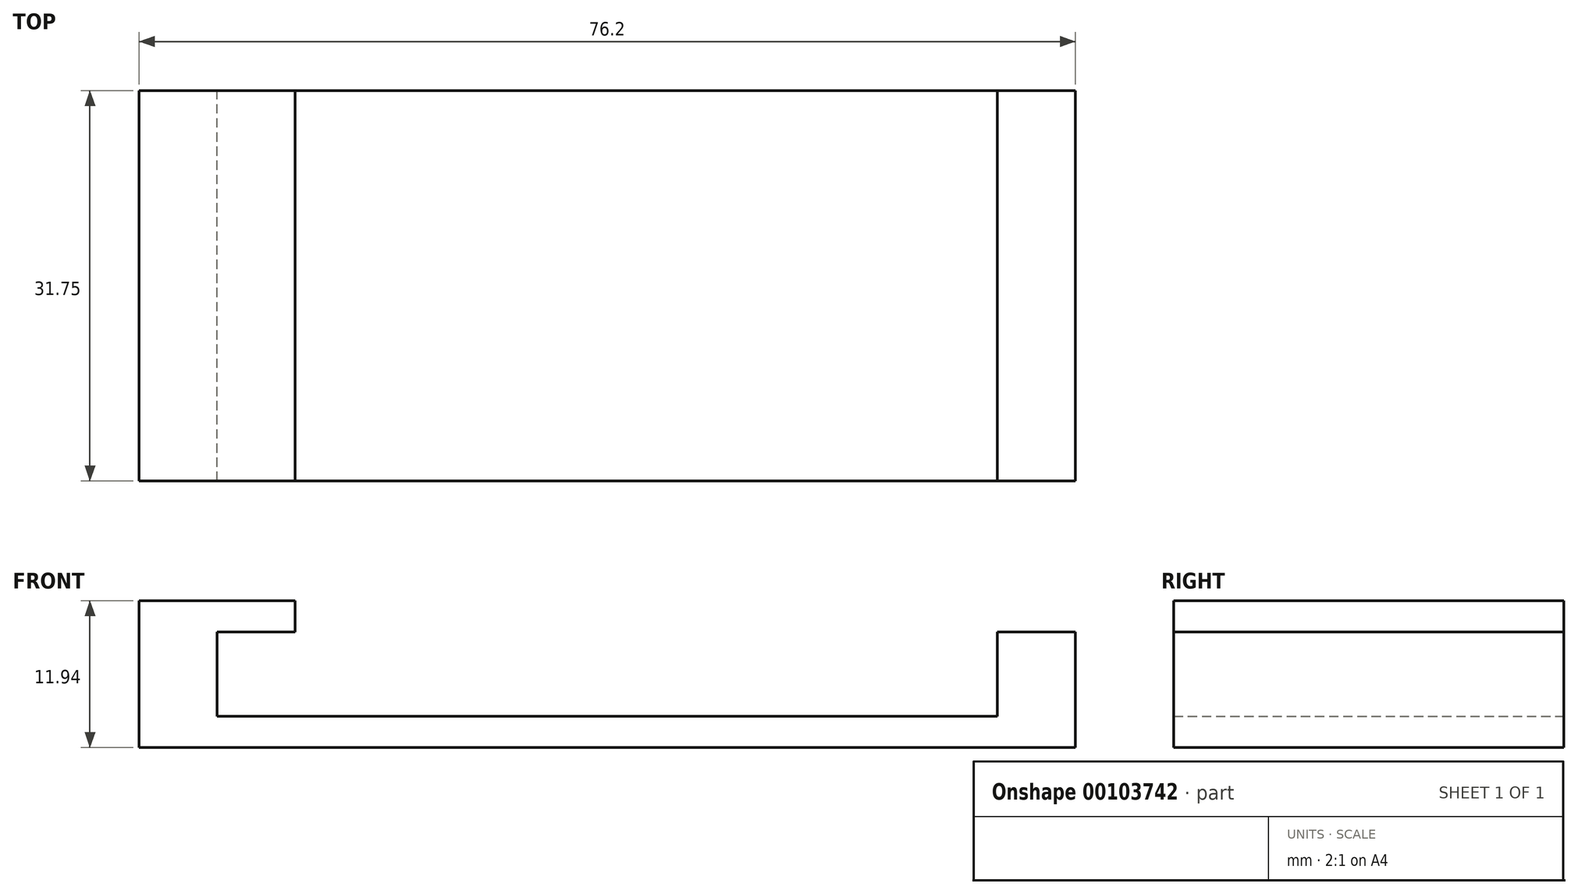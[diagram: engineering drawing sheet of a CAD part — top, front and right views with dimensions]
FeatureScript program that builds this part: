
annotation { "Feature Type Name" : "Feature", "Feature Type Description" : "" }
export const myFeature = defineFeature(function(context is Context, id is Id, definition is map)
    precondition{}
    {
        {
            var Q0;
            Q0=qCreatedBy(makeId("Top.planeOp"),FACE);
            var sketch = newSketch(context, id + "F0", { "sketchPlane" : qUnion([Q0])});
            skLineSegment(sketch, "E0.bottom", {"start": v(-31.75, 31.75) * mm, "end": v(31.75, 31.75) * mm});
            skLineSegment(sketch, "E0.top", {"start": v(-31.75, 0) * mm, "end": v(31.75, 0) * mm});
            skLineSegment(sketch, "E0.left", {"start": v(-31.75, 31.75) * mm, "end": v(-31.75, 0) * mm});
            skLineSegment(sketch, "E0.right", {"start": v(31.75, 31.75) * mm, "end": v(31.75, 0) * mm});
            skLineSegment(sketch, "E1.0", {"start": v(38.1, 31.75) * mm, "end": v(38.1, 0) * mm});
            skLineSegment(sketch, "E2.0", {"start": v(-38.1, 31.75) * mm, "end": v(-38.1, 0) * mm});
            skLineSegment(sketch, "E3", {"start": v(-38.1, 31.75) * mm, "end": v(-31.75, 31.75) * mm});
            skLineSegment(sketch, "E4", {"start": v(-38.1, 0) * mm, "end": v(-31.75, 0) * mm});
            skLineSegment(sketch, "E5", {"start": v(31.75, 0) * mm, "end": v(38.1, 0) * mm});
            skLineSegment(sketch, "E6", {"start": v(31.75, 31.75) * mm, "end": v(38.1, 31.75) * mm});
            skPoint(sketch, "E7", {"position": v(-38.1, 15.87) * mm});
            skPoint(sketch, "E8", {"position": v(-31.75, 15.87) * mm});
            skSolve(sketch);
        }
        {
            var Q0;
            Q0=makeQuery(id+"F0.imprint","IMPRINT",FACE,{"disambiguationData":[TD([[makeQuery(id+"F0.imprint","IMPRINT",EDGE,{"derivedFrom":sQuery(id+"F0.wireOp",EDGE,"E0.left")}),-1.0]])]});
            var Q1;
            Q1=makeQuery(id+"F0.imprint","IMPRINT",FACE,{"disambiguationData":[TD([[makeQuery(id+"F0.imprint","IMPRINT",EDGE,{"derivedFrom":sQuery(id+"F0.wireOp",EDGE,"E0.bottom")}),-1.0]])]});
            var Q2;
            Q2=makeQuery(id+"F0.imprint","IMPRINT",FACE,{"disambiguationData":[TD([[makeQuery(id+"F0.imprint","IMPRINT",EDGE,{"derivedFrom":sQuery(id+"F0.wireOp",EDGE,"E0.right")}),1.0]])]});
            extrude(context, id + "F1", {"entities" : qUnion([Q0, Q1, Q2]), "depth" : 2.54 * mm});
        }
        {
            var Q0;
            Q0=makeQuery(id+"F0.imprint","IMPRINT",FACE,{"disambiguationData":[TD([[makeQuery(id+"F0.imprint","IMPRINT",EDGE,{"derivedFrom":sQuery(id+"F0.wireOp",EDGE,"E0.left")}),-1.0]])]});
            var Q1;
            Q1=makeQuery(id+"F0.imprint","IMPRINT",FACE,{"disambiguationData":[TD([[makeQuery(id+"F0.imprint","IMPRINT",EDGE,{"derivedFrom":sQuery(id+"F0.wireOp",EDGE,"E0.right")}),1.0]])]});
            extrude(context, id + "F2", {"entities" : qUnion([Q0, Q1]), "operationType" : NewBodyOperationType.ADD, "depth" : 9.4 * mm});
        }
        {
            var Q0;
            Q0=makeQuery(id+"F2.opExtrude","CAP_FACE",FACE,{"disambiguationData":[OSD([sQuery(id+"F0.wireOp",EDGE,"E0.left"),sQuery(id+"F0.wireOp",EDGE,"E2.0"),sQuery(id+"F0.wireOp",EDGE,"E3"),sQuery(id+"F0.wireOp",EDGE,"E4")])],"isStart":false});
            var sketch = newSketch(context, id + "F3", { "sketchPlane" : qUnion([Q0])});
            skLineSegment(sketch, "E9.bottom", {"start": v(-38.1, 31.75) * mm, "end": v(-25.4, 31.75) * mm});
            skLineSegment(sketch, "E9.top", {"start": v(-38.1, 0) * mm, "end": v(-25.4, 0) * mm});
            skLineSegment(sketch, "E9.left", {"start": v(-38.1, 31.75) * mm, "end": v(-38.1, 0) * mm});
            skLineSegment(sketch, "E9.right", {"start": v(-25.4, 31.75) * mm, "end": v(-25.4, 0) * mm});
            skSolve(sketch);
        }
        {
            var Q0;
            {var subQ2=sQuery(id+"F3.wireOp",EDGE,"E9.right");Q0=makeQuery(id+"F3.imprint","IMPRINT",FACE,{"disambiguationData":[TD([[makeQuery(id+"F3.imprint","IMPRINT",EDGE,{"derivedFrom":subQ2}),-1.0]])]});}
            var Q1;
            {var subQ2=sQuery(id+"F3.wireOp",EDGE,"E9.left");Q1=makeQuery(id+"F3.imprint","IMPRINT",FACE,{"disambiguationData":[TD([[makeQuery(id+"F3.imprint","IMPRINT",EDGE,{"derivedFrom":subQ2}),1.0]])]});}
            extrude(context, id + "F4", {"entities" : qUnion([Q0, Q1]), "operationType" : NewBodyOperationType.ADD, "depth" : 2.54 * mm});
        }
    });
